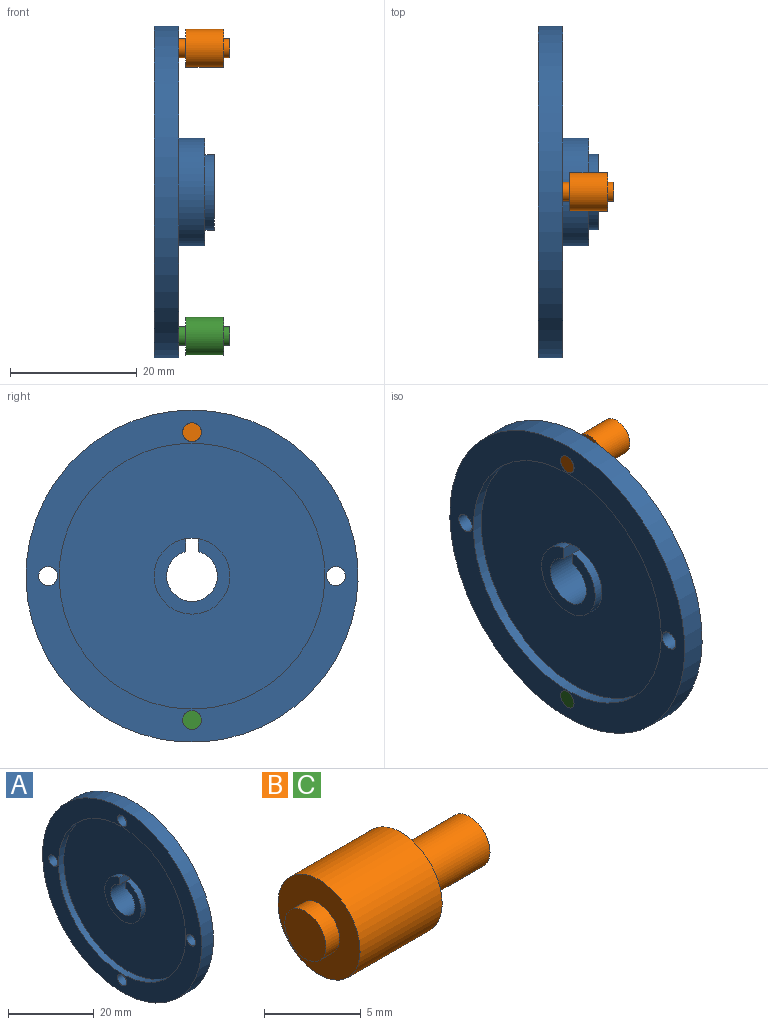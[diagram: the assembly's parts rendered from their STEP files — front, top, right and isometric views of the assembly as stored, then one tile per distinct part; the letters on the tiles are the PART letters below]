
ASSEMBLY  parts=3 mates=1
PART A: 19 faces, bbox 9.5x52.5x52.5 mm
  f0: cylinder r=6mm len=12mm, axis (-1,0,0), area 53.5mm2, adj f1,f6,f17,f18
  f1: plane 17x17mm, normal (1,0,0), area 113.8mm2, adj f0,f7,f16,f17,f18
  f2: plane 42x42mm, normal (-1,0,0), area 1272.3mm2, adj f3,f11,f16,f17,f18
  f3: cylinder r=6mm len=12mm, axis (-1,0,0), area 53.5mm2, adj f2,f4,f17,f18
  f4: plane 12x11.92mm, normal (-1,0,0), area 58.8mm2, adj f3,f5,f17,f18
  f5: cylinder r=4mm len=9.29mm, axis (-1,0,0), area 214.7mm2, adj f4,f6,f17,f18
  f6: plane 12x11.92mm, normal (1,0,0), area 58.8mm2, adj f0,f5,f17,f18
  f7: cylinder r=8.5mm len=17mm, axis (-1,0,0), area 221.5mm2, adj f1,f8
  f8: plane 52.48x52.48mm, normal (1,0,0), area 1908.2mm2, adj f7,f9,f12,f13,f14,f15
  f9: cylinder r=26.24mm len=52.48mm, axis (-1,0,0), area 641.7mm2, adj f8,f10
  f10: plane 52.48x52.48mm, normal (-1,0,0), area 749.7mm2, adj f9,f11,f12,f13,f14,f15
  f11: cylinder r=21mm len=42mm, axis (-1,0,0), area 230.9mm2, adj f2,f10
  f12: cylinder r=1.5mm len=3.89mm, axis (-1,0,0), area 36.7mm2, adj f8,f10
  f13: cylinder r=1.5mm len=3.89mm, axis (-1,0,0), area 36.7mm2, adj f8,f10
  f14: cylinder r=1.5mm len=3.89mm, axis (-1,0,0), area 36.7mm2, adj f8,f10
  f15: cylinder r=1.5mm len=3.89mm, axis (-1,0,0), area 36.7mm2, adj f8,f10
  f16: plane 6.29x2mm, normal (0,0,-1), area 12.6mm2, adj f1,f2,f17,f18
  f17: plane 9.29x2.13mm, normal (0,1,0), area 19.5mm2, adj f0,f1,f2,f3,f4,f5,f6,f16
  f18: plane 9.29x2.13mm, normal (0,-1,0), area 19.5mm2, adj f0,f1,f2,f3,f4,f5,f6,f16
PART B: 7 faces, bbox 12x6x6 mm
  f0: cylinder r=3mm len=6mm, axis (-1,0,0), area 113.1mm2, adj f1,f6
  f1: plane 6x6mm, normal (-1,0,0), area 21.2mm2, adj f0,f2
  f2: cylinder r=1.5mm len=3mm, axis (-1,0,0), area 9.4mm2, adj f1,f3
  f3: plane 3x3mm, normal (-1,0,0), area 7.1mm2, adj f2
  f4: plane 3x3mm, normal (1,0,0), area 7.1mm2, adj f5
  f5: cylinder r=1.5mm len=5mm, axis (-1,0,0), area 47.1mm2, adj f4,f6
  f6: plane 6x6mm, normal (1,0,0), area 21.2mm2, adj f0,f5
PART C: same geometry as B
PLACE A t=(-5.65,0,0)mm
PLACE B rot(axis=(0,1,0),180deg) t=(-9.54,0,22.74)mm
PLACE C rot(axis=(0,0,1),180deg) t=(-9.54,0,-22.74)mm
MATE revolute B.f0 <-> A.f13  axis (-1,0,0) through (-9.54,0,22.74)mm
